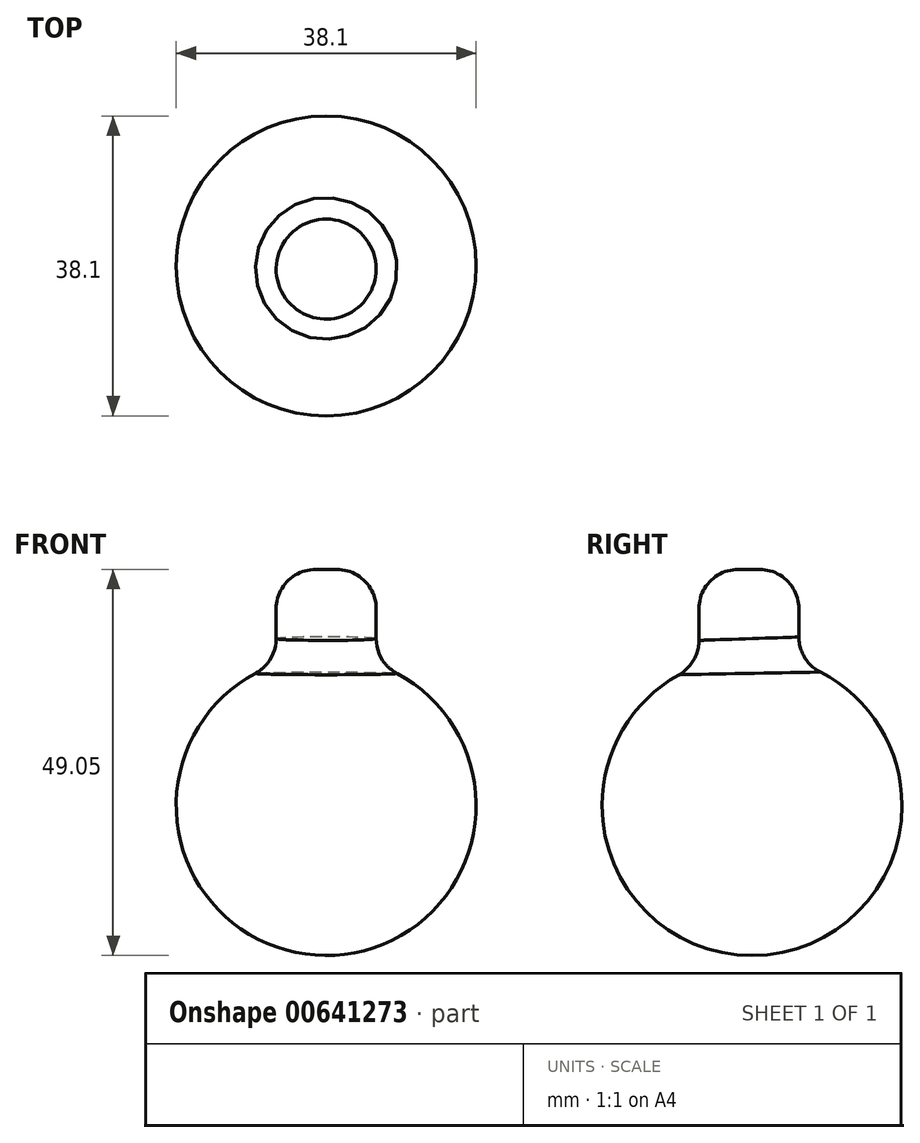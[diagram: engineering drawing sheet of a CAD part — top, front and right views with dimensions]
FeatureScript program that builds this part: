
annotation { "Feature Type Name" : "Feature", "Feature Type Description" : "" }
export const myFeature = defineFeature(function(context is Context, id is Id, definition is map)
    precondition{}
    {
        {
            var Q0;
            Q0=qCreatedBy(makeId("Top.planeOp"),FACE);
            var sketch = newSketch(context, id + "F0", { "sketchPlane" : qUnion([Q0])});
            skCircle(sketch, "E0", {"center": v(0, 0) * mm, "radius": 6.35 * mm});
            skSolve(sketch);
        }
        {
            var Q0;
            Q0=qCreatedBy(makeId("Top.planeOp"),FACE);
            var sketch = newSketch(context, id + "F1", { "sketchPlane" : qUnion([Q0])});
            skArc(sketch, "E1", {"start": v(0, -18.65) * mm, "mid": v(19.05, 0.4) * mm, "end": v(0, 19.45) * mm});
            skLineSegment(sketch, "E2", {"start": v(0, -18.65) * mm, "end": v(0, 19.45) * mm});
            skSolve(sketch);
        }
        {
            var Q0;
            Q0 = qSketchRegion(id + "F1", true);
            var Q1;
            Q1=sQuery(id+"F1.wireOp",EDGE,"E2");
            revolve(context, id + "F2", {"entities" : qUnion([Q0]), "axis" : qUnion([Q1]), "revolveType" : RevolveType.FULL});
        }
        {
            var Q0;
            Q0 = qSketchRegion(id + "F0", true);
            extrude(context, id + "F3", {"entities" : qUnion([Q0]), "operationType" : NewBodyOperationType.ADD, "depth" : 30 * mm, "offsetDistance" : 25 * mm});
        }
        {
            var Q0;
            Q0=makeQuery(id+"F3.boolean.opBoolean","INTERSECT",EDGE,{"derivedFrom":[makeQuery(id+"F2.opRevolve","SWEPT_FACE",FACE,{"disambiguationData":[OSD([sQuery(id+"F1.wireOp",EDGE,"E1")])]}),makeQuery(id+"F3.opExtrude","SWEPT_FACE",FACE,{"disambiguationData":[OSD([sQuery(id+"F0.wireOp",EDGE,"E0")])]})]});
            var Q1;
            Q1=makeQuery(id+"F3.opExtrude","CAP_EDGE",EDGE,{"disambiguationData":[OSD([sQuery(id+"F0.wireOp",EDGE,"E0")])],"isStart":false});
            fillet(context, id + "F4", {"entities" : qUnion([Q0, Q1]), "radius" : 5 * mm, "tangentPropagation" : true, "allowEdgeOverflow" : false});
        }
    });
